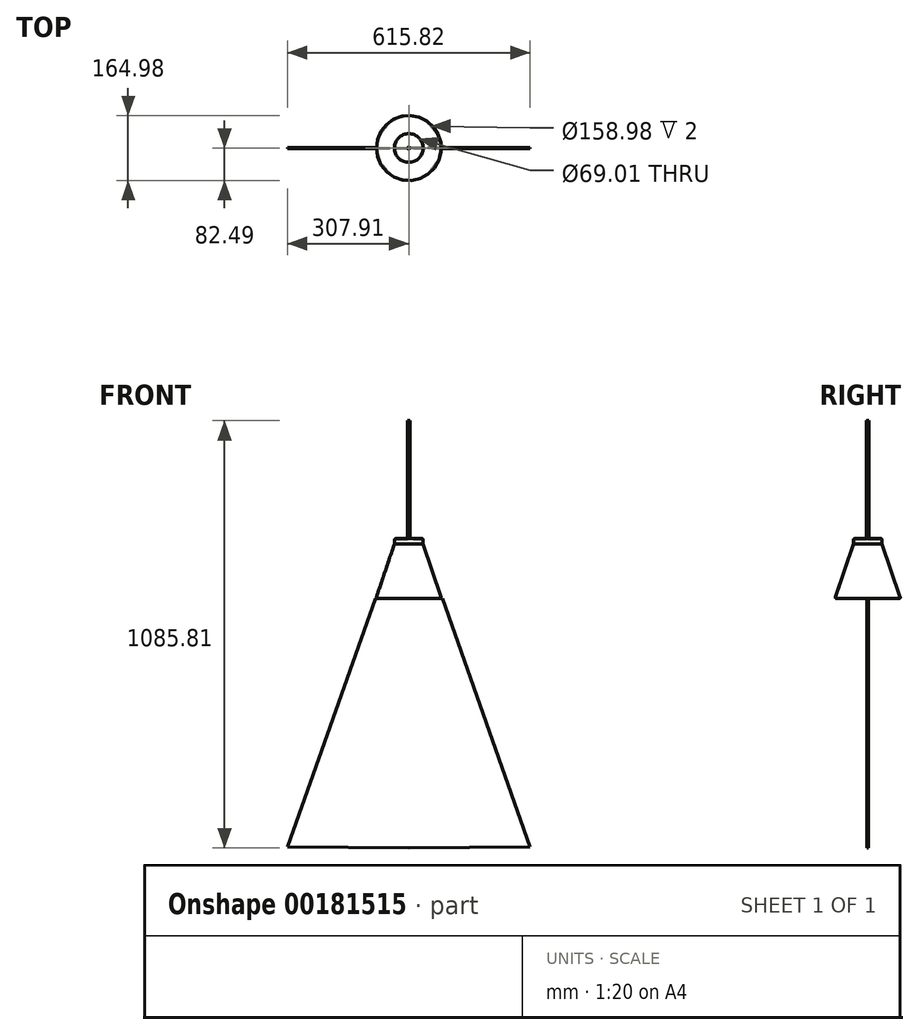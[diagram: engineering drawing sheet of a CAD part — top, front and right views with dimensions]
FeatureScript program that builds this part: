
annotation { "Feature Type Name" : "Feature", "Feature Type Description" : "" }
export const myFeature = defineFeature(function(context is Context, id is Id, definition is map)
    precondition{}
    {
        {
            var Q0;
            Q0=qCreatedBy(makeId("Front.planeOp"),FACE);
            var sketch = newSketch(context, id + "F0", { "sketchPlane" : qUnion([Q0])});
            skLineSegment(sketch, "E0", {"start": v(0, 0) * mm, "end": v(0, 496.42) * mm, "construction": true});
            skLineSegment(sketch, "E1", {"start": v(0, 286.04) * mm, "end": v(33.5, 286.04) * mm});
            skLineSegment(sketch, "E2", {"start": v(36.5, 283.04) * mm, "end": v(36.5, 273.07) * mm});
            skLineSegment(sketch, "E3", {"start": v(36.5, 273.07) * mm, "end": v(82.33, 137.6) * mm});
            skLineSegment(sketch, "E4", {"start": v(79.5, 133.64) * mm, "end": v(0, 133.64) * mm});
            skLineSegment(sketch, "E5", {"start": v(83.67, 133.64) * mm, "end": v(402.1, -501.54) * mm, "construction": true});
            skPoint(sketch, "E6.visualSharp", {"position": v(83.67, 133.64) * mm});
            skArc(sketch, "E6.filletArc", {"start": v(79.5, 133.64) * mm, "mid": v(81.93, 134.9) * mm, "end": v(82.33, 137.6) * mm});
            skPoint(sketch, "E7.visualSharp", {"position": v(36.5, 286.04) * mm});
            skArc(sketch, "E7.filletArc", {"start": v(36.5, 283.04) * mm, "mid": v(35.63, 285.16) * mm, "end": v(33.5, 286.04) * mm});
            skLineSegment(sketch, "E8", {"start": v(0, 286.04) * mm, "end": v(0, 133.64) * mm});
            skSolve(sketch);
        }
        {
            var Q0;
            Q0=makeQuery(id+"F0.imprint","IMPRINT",FACE,{"disambiguationData":[TD([[makeQuery(id+"F0.imprint","IMPRINT",EDGE,{"derivedFrom":sQuery(id+"F0.wireOp",EDGE,"E1")}),-1.0]])]});
            var Q1;
            Q1=sQuery(id+"F0.wireOp",EDGE,"E0");
            revolve(context, id + "F1", {"entities" : qUnion([Q0]), "axis" : qUnion([Q1]), "revolveType" : RevolveType.FULL});
        }
        {
            var Q0;
            Q0=makeQuery(id+"F1.opRevolve","SWEPT_FACE",FACE,{"disambiguationData":[OSD([sQuery(id+"F0.wireOp",EDGE,"E4")])]});
            shell(context, id + "F2", {"entities" : qUnion([Q0]), "thickness" : 2 * mm});
        }
        {
            var Q0;
            Q0=makeQuery(id+"F1.opRevolve","SWEPT_FACE",FACE,{"disambiguationData":[OSD([sQuery(id+"F0.wireOp",EDGE,"E1")])]});
            var sketch = newSketch(context, id + "F3", { "sketchPlane" : qUnion([Q0])});
            skCircle(sketch, "E9", {"center": v(0, 0) * mm, "radius": 3 * mm});
            skSolve(sketch);
        }
        {
            var Q0;
            Q0=makeQuery(id+"F3.imprint","IMPRINT",FACE,{"disambiguationData":[TD([[makeQuery(id+"F3.imprint","IMPRINT",EDGE,{"derivedFrom":sQuery(id+"F3.wireOp",EDGE,"E9")}),1.0]])]});
            extrude(context, id + "F4", {"entities" : qUnion([Q0]), "operationType" : NewBodyOperationType.ADD, "depth" : 300 * mm});
        }
        {
            var Q0;
            Q0=qCreatedBy(makeId("Front.planeOp"),FACE);
            var sketch = newSketch(context, id + "F5", { "sketchPlane" : qUnion([Q0])});
            skLineSegment(sketch, "E10", {"start": v(0, 501.06) * mm, "end": v(0, -499.77) * mm, "construction": true});
            skLineSegment(sketch, "E11", {"start": v(0, 133.69) * mm, "end": v(85.13, 133.69) * mm});
            skLineSegment(sketch, "E12", {"start": v(85.13, 133.69) * mm, "end": v(307.9, -497.16) * mm});
            skLineSegment(sketch, "E13", {"start": v(307.9, -497.16) * mm, "end": v(0, -499.77) * mm});
            skLineSegment(sketch, "E14.MirrorCS", {"start": v(0, 133.69) * mm, "end": v(-85.13, 133.69) * mm});
            skLineSegment(sketch, "E15.MirrorCS", {"start": v(-85.13, 133.69) * mm, "end": v(-307.9, -497.16) * mm});
            skLineSegment(sketch, "E16.MirrorCS", {"start": v(-307.9, -497.16) * mm, "end": v(0, -499.77) * mm});
            skSolve(sketch);
        }
        {
            var Q0;
            Q0=makeQuery(id+"F5.imprint","IMPRINT",FACE,{"disambiguationData":[TD([[makeQuery(id+"F5.imprint","IMPRINT",EDGE,{"derivedFrom":sQuery(id+"F5.wireOp",EDGE,"E11")}),-1.0]])]});
            extrude(context, id + "F6", {"entities" : qUnion([Q0]), "operationType" : NewBodyOperationType.ADD, "endBound" : BoundingType.SYMMETRIC, "depth" : 3 * mm});
        }
    });
